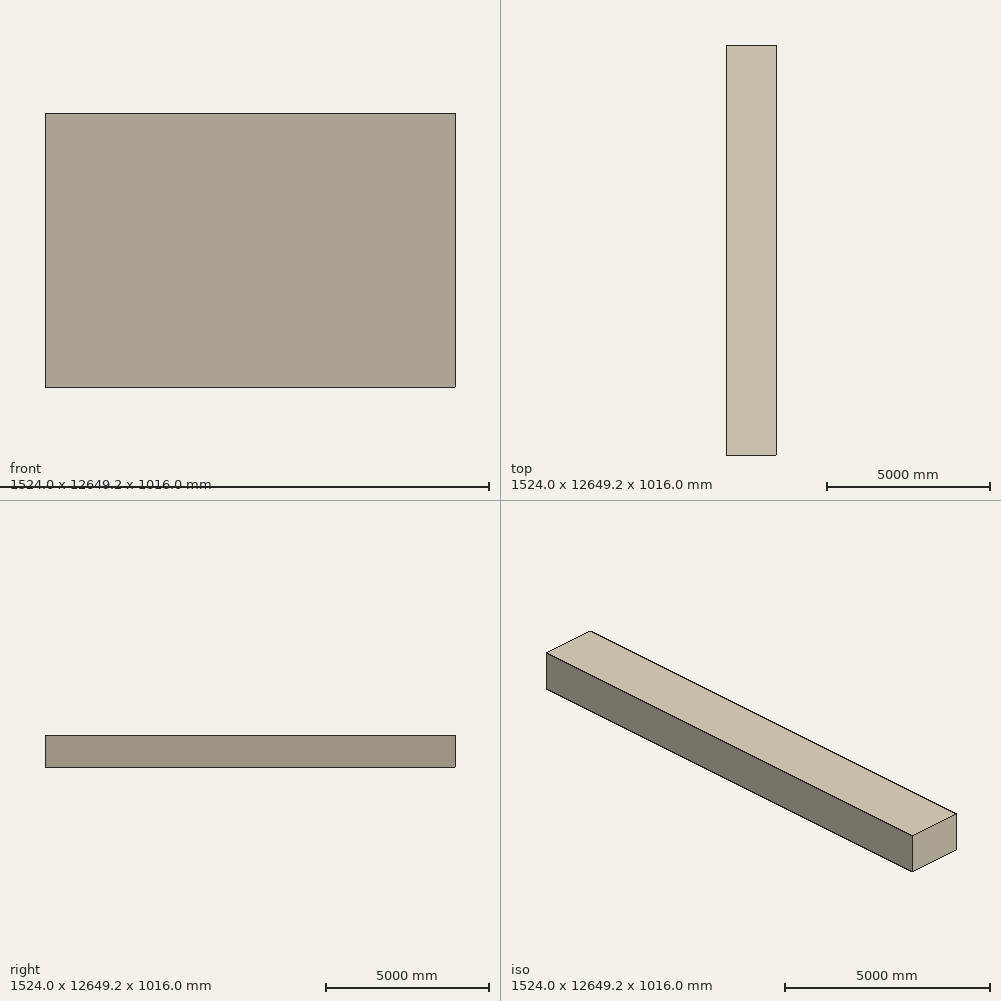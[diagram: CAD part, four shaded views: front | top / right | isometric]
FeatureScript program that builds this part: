
annotation { "Feature Type Name" : "Feature", "Feature Type Description" : "" }
export const myFeature = defineFeature(function(context is Context, id is Id, definition is map)
    precondition{}
    {
        {
            var Q0;
            Q0=qCreatedBy(makeId("Front.planeOp"),FACE);
            var sketch = newSketch(context, id + "F0", { "sketchPlane" : qUnion([Q0])});
            skLineSegment(sketch, "E0.bottom", {"start": v(-762, 508) * mm, "end": v(762, 508) * mm});
            skLineSegment(sketch, "E0.top", {"start": v(-762, -508) * mm, "end": v(762, -508) * mm});
            skLineSegment(sketch, "E0.left", {"start": v(-762, 508) * mm, "end": v(-762, -508) * mm});
            skLineSegment(sketch, "E0.right", {"start": v(762, 508) * mm, "end": v(762, -508) * mm});
            skSolve(sketch);
        }
        {
            var Q0;
            Q0=makeQuery(id+"F0.imprint","IMPRINT",FACE,{"disambiguationData":[TD([[makeQuery(id+"F0.imprint","IMPRINT",EDGE,{"derivedFrom":sQuery(id+"F0.wireOp",EDGE,"E0.bottom")}),-1.0]])]});
            extrude(context, id + "F1", {"entities" : qUnion([Q0]), "depth" : 12649.2 * mm, "offsetDistance" : 25.4 * mm, "symmetric" : true});
        }
    });
